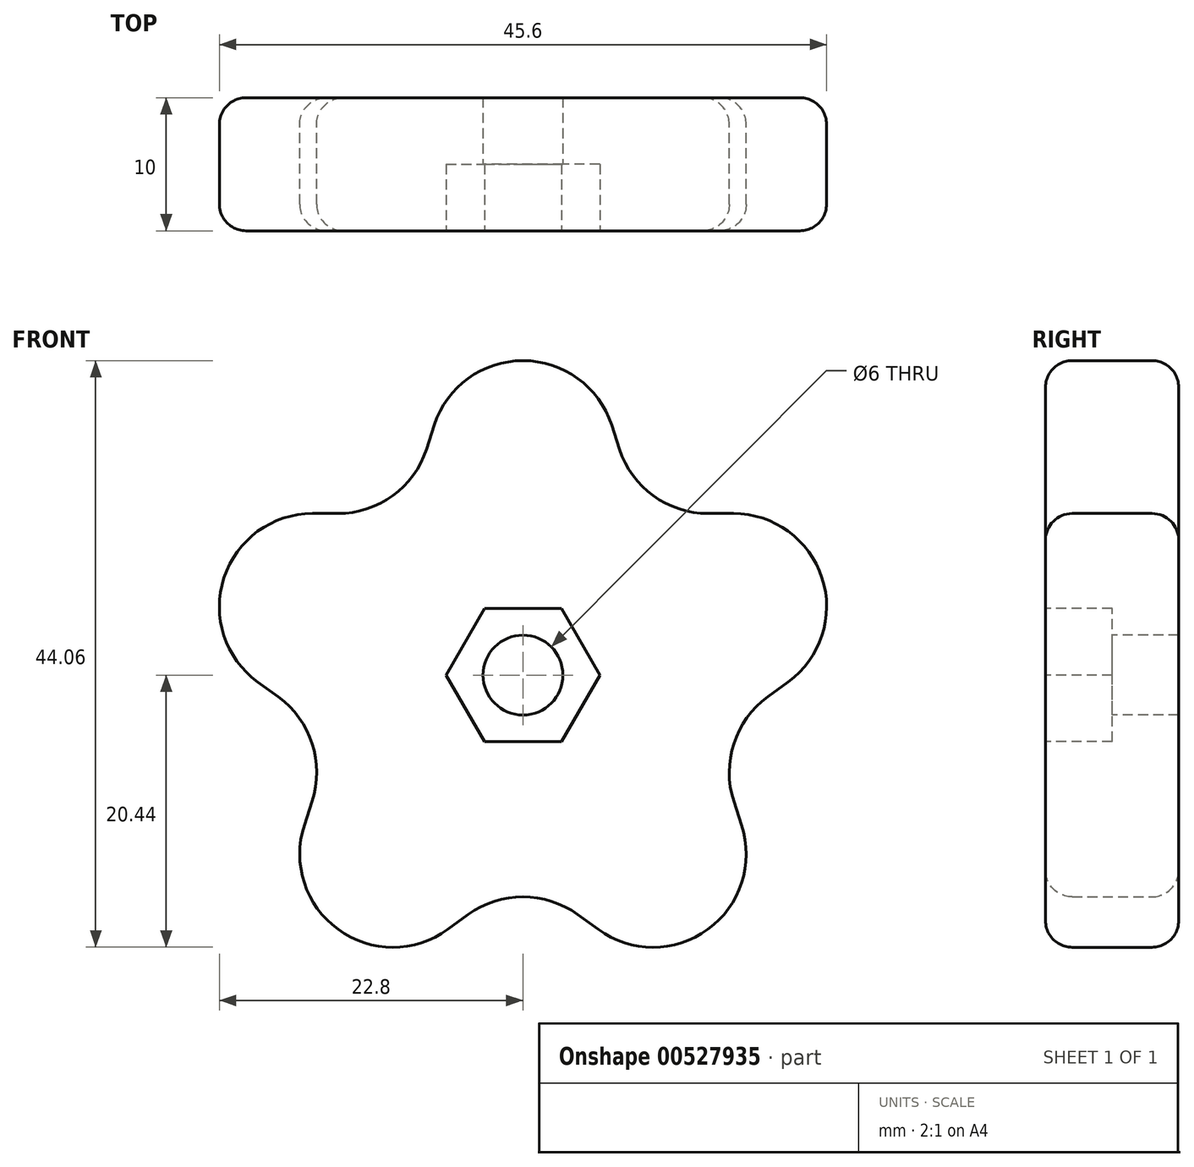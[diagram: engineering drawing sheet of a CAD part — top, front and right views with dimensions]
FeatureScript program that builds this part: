
annotation { "Feature Type Name" : "Feature", "Feature Type Description" : "" }
export const myFeature = defineFeature(function(context is Context, id is Id, definition is map)
    precondition{}
    {
        {
            var Q0;
            Q0=qCreatedBy(makeId("Front.planeOp"),FACE);
            var sketch = newSketch(context, id + "F0", { "sketchPlane" : qUnion([Q0])});
            skCircle(sketch, "E0.cCircle", {"center": v(0, 0) * mm, "radius": 39.27 * mm, "construction": true});
            skLineSegment(sketch, "E1", {"start": v(0, 39.27) * mm, "end": v(-8.82, 12.14) * mm});
            skLineSegment(sketch, "E2", {"start": v(-37.35, 12.14) * mm, "end": v(-8.82, 12.14) * mm});
            skLineSegment(sketch, "E3", {"start": v(0, 39.27) * mm, "end": v(8.82, 12.14) * mm});
            skLineSegment(sketch, "E4", {"start": v(23.08, -31.77) * mm, "end": v(0, -15) * mm});
            skLineSegment(sketch, "E5", {"start": v(-23.08, -31.77) * mm, "end": v(0, -15) * mm});
            skLineSegment(sketch, "E6.trimOffspring", {"start": v(-14.27, -4.64) * mm, "end": v(-37.35, 12.14) * mm});
            skLineSegment(sketch, "E7.trimOffspring", {"start": v(14.27, -4.64) * mm, "end": v(37.35, 12.14) * mm});
            skLineSegment(sketch, "E8.trimOffspring", {"start": v(14.27, -4.64) * mm, "end": v(23.08, -31.77) * mm});
            skLineSegment(sketch, "E9.trimOffspring", {"start": v(8.82, 12.14) * mm, "end": v(37.35, 12.14) * mm});
            skLineSegment(sketch, "E10.trimOffspring", {"start": v(-14.27, -4.64) * mm, "end": v(-23.08, -31.77) * mm});
            skCircle(sketch, "E11", {"center": v(0, 0) * mm, "radius": 15 * mm});
            skSolve(sketch);
        }
        {
            var Q0;
            {var subQ0=sQuery(id+"F0.wireOp",EDGE,"E7.trimOffspring");Q0=makeQuery(id+"F0.imprint","IMPRINT",FACE,{"disambiguationData":[TD([[makeQuery(id+"F0.imprint","IMPRINT",EDGE,{"derivedFrom":subQ0}),1.0]])]});}
            var Q1;
            {var subQ0=sQuery(id+"F0.wireOp",EDGE,"E1");Q1=makeQuery(id+"F0.imprint","IMPRINT",FACE,{"disambiguationData":[TD([[makeQuery(id+"F0.imprint","IMPRINT",EDGE,{"derivedFrom":subQ0}),1.0]])]});}
            var Q2;
            {var subQ0=sQuery(id+"F0.wireOp",EDGE,"E2");Q2=makeQuery(id+"F0.imprint","IMPRINT",FACE,{"disambiguationData":[TD([[makeQuery(id+"F0.imprint","IMPRINT",EDGE,{"derivedFrom":subQ0}),-1.0]])]});}
            var Q3;
            {var subQ0=sQuery(id+"F0.wireOp",EDGE,"E11");var subQ4=makeQuery(id+"F0.imprint","INTERSECT",VERTEX,{"derivedFrom":[sQuery(id+"F0.wireOp",EDGE,"E1"),sQuery(id+"F0.wireOp",EDGE,"E2"),subQ0]});Q3=makeQuery(id+"F0.imprint","IMPRINT",FACE,{"disambiguationData":[TD([[makeQuery(id+"F0.imprint","IMPRINT",EDGE,{"disambiguationData":[TD([[subQ4,1.0]])],"derivedFrom":subQ0}),1.0]])]});}
            var Q4;
            {var subQ0=sQuery(id+"F0.wireOp",EDGE,"E5");Q4=makeQuery(id+"F0.imprint","IMPRINT",FACE,{"disambiguationData":[TD([[makeQuery(id+"F0.imprint","IMPRINT",EDGE,{"derivedFrom":subQ0}),1.0]])]});}
            var Q5;
            {var subQ0=sQuery(id+"F0.wireOp",EDGE,"E4");Q5=makeQuery(id+"F0.imprint","IMPRINT",FACE,{"disambiguationData":[TD([[makeQuery(id+"F0.imprint","IMPRINT",EDGE,{"derivedFrom":subQ0}),-1.0]])]});}
            extrude(context, id + "F1", {"entities" : qUnion([Q0, Q1, Q2, Q3, Q4, Q5]), "depth" : 10 * mm, "offsetDistance" : 25 * mm});
        }
        {
            var Q0;
            Q0=makeQuery(id+"F1.opExtrude","SWEPT_EDGE",EDGE,{"disambiguationData":[OSD([sQuery(id+"F0.wireOp",EDGE,"E1"),sQuery(id+"F0.wireOp",EDGE,"E3")])]});
            var Q1;
            Q1=makeQuery(id+"F1.opExtrude","SWEPT_EDGE",EDGE,{"disambiguationData":[OSD([sQuery(id+"F0.wireOp",EDGE,"E7.trimOffspring"),sQuery(id+"F0.wireOp",EDGE,"E9.trimOffspring")])]});
            var Q2;
            Q2=makeQuery(id+"F1.opExtrude","SWEPT_EDGE",EDGE,{"disambiguationData":[OSD([sQuery(id+"F0.wireOp",EDGE,"E4"),sQuery(id+"F0.wireOp",EDGE,"E8.trimOffspring")])]});
            var Q3;
            Q3=makeQuery(id+"F1.opExtrude","SWEPT_EDGE",EDGE,{"disambiguationData":[OSD([sQuery(id+"F0.wireOp",EDGE,"E2"),sQuery(id+"F0.wireOp",EDGE,"E6.trimOffspring")])]});
            var Q4;
            Q4=makeQuery(id+"F1.opExtrude","SWEPT_EDGE",EDGE,{"disambiguationData":[OSD([sQuery(id+"F0.wireOp",EDGE,"E5"),sQuery(id+"F0.wireOp",EDGE,"E10.trimOffspring")])]});
            var Q5;
            Q5=makeQuery(id+"F1.opExtrude","SWEPT_EDGE",EDGE,{"disambiguationData":[OSD([sQuery(id+"F0.wireOp",EDGE,"E6.trimOffspring"),sQuery(id+"F0.wireOp",EDGE,"E10.trimOffspring"),sQuery(id+"F0.wireOp",EDGE,"E11")])]});
            var Q6;
            Q6=makeQuery(id+"F1.opExtrude","SWEPT_EDGE",EDGE,{"disambiguationData":[OSD([sQuery(id+"F0.wireOp",EDGE,"E4"),sQuery(id+"F0.wireOp",EDGE,"E5"),sQuery(id+"F0.wireOp",EDGE,"E11")])]});
            var Q7;
            Q7=makeQuery(id+"F1.opExtrude","SWEPT_EDGE",EDGE,{"disambiguationData":[OSD([sQuery(id+"F0.wireOp",EDGE,"E7.trimOffspring"),sQuery(id+"F0.wireOp",EDGE,"E8.trimOffspring"),sQuery(id+"F0.wireOp",EDGE,"E11")])]});
            var Q8;
            Q8=makeQuery(id+"F1.opExtrude","SWEPT_EDGE",EDGE,{"disambiguationData":[OSD([sQuery(id+"F0.wireOp",EDGE,"E3"),sQuery(id+"F0.wireOp",EDGE,"E9.trimOffspring"),sQuery(id+"F0.wireOp",EDGE,"E11")])]});
            var Q9;
            Q9=makeQuery(id+"F1.opExtrude","SWEPT_EDGE",EDGE,{"disambiguationData":[OSD([sQuery(id+"F0.wireOp",EDGE,"E1"),sQuery(id+"F0.wireOp",EDGE,"E2"),sQuery(id+"F0.wireOp",EDGE,"E11")])]});
            fillet(context, id + "F2", {"entities" : qUnion([Q0, Q1, Q2, Q3, Q4, Q5, Q6, Q7, Q8, Q9]), "radius" : 7 * mm, "tangentPropagation" : true, "allowEdgeOverflow" : false});
        }
        {
            var Q0;
            Q0=makeQuery(id+"F1.opExtrude","CAP_FACE",FACE,{"disambiguationData":[OSD([sQuery(id+"F0.wireOp",EDGE,"E1"),sQuery(id+"F0.wireOp",EDGE,"E2"),sQuery(id+"F0.wireOp",EDGE,"E3"),sQuery(id+"F0.wireOp",EDGE,"E4"),sQuery(id+"F0.wireOp",EDGE,"E5"),sQuery(id+"F0.wireOp",EDGE,"E6.trimOffspring"),sQuery(id+"F0.wireOp",EDGE,"E7.trimOffspring"),sQuery(id+"F0.wireOp",EDGE,"E8.trimOffspring"),sQuery(id+"F0.wireOp",EDGE,"E9.trimOffspring"),sQuery(id+"F0.wireOp",EDGE,"E10.trimOffspring")])],"isStart":false});
            var sketch = newSketch(context, id + "F3", { "sketchPlane" : qUnion([Q0])});
            skCircle(sketch, "E12.cCircle", {"center": v(0, 0) * mm, "radius": 5 * mm, "construction": true});
            skLineSegment(sketch, "E12.0", {"start": v(-2.89, 5) * mm, "end": v(2.89, 5) * mm});
            skLineSegment(sketch, "E12.1", {"start": v(2.89, 5) * mm, "end": v(5.77, 0) * mm});
            skLineSegment(sketch, "E12.2", {"start": v(5.77, 0) * mm, "end": v(2.89, -5) * mm});
            skLineSegment(sketch, "E12.3", {"start": v(2.89, -5) * mm, "end": v(-2.89, -5) * mm});
            skLineSegment(sketch, "E12.4", {"start": v(-2.89, -5) * mm, "end": v(-5.77, 0) * mm});
            skLineSegment(sketch, "E12.5", {"start": v(-5.77, 0) * mm, "end": v(-2.89, 5) * mm});
            skPoint(sketch, "E12.0.midPoint", {"position": v(0, 5) * mm});
            skSolve(sketch);
        }
        {
            var Q0;
            Q0=makeQuery(id+"F3.imprint","IMPRINT",FACE,{"disambiguationData":[TD([[makeQuery(id+"F3.imprint","IMPRINT",EDGE,{"derivedFrom":sQuery(id+"F3.wireOp",EDGE,"E12.0")}),-1.0]])]});
            extrude(context, id + "F4", {"entities" : qUnion([Q0]), "operationType" : NewBodyOperationType.REMOVE, "oppositeDirection" : true, "depth" : 5 * mm, "offsetDistance" : 25 * mm});
        }
        {
            var Q0;
            Q0=makeQuery(id+"F4.boolean.opBoolean","COPY",FACE,{"derivedFrom":makeQuery(id+"F4.opExtrude","CAP_FACE",FACE,{"disambiguationData":[OSD([sQuery(id+"F3.wireOp",EDGE,"E12.0"),sQuery(id+"F3.wireOp",EDGE,"E12.1"),sQuery(id+"F3.wireOp",EDGE,"E12.2"),sQuery(id+"F3.wireOp",EDGE,"E12.3"),sQuery(id+"F3.wireOp",EDGE,"E12.4"),sQuery(id+"F3.wireOp",EDGE,"E12.5")])],"isStart":false})});
            var sketch = newSketch(context, id + "F5", { "sketchPlane" : qUnion([Q0])});
            skCircle(sketch, "E13", {"center": v(0, 0) * mm, "radius": 3 * mm});
            skSolve(sketch);
        }
        {
            var Q0;
            Q0=makeQuery(id+"F5.imprint","IMPRINT",FACE,{"disambiguationData":[TD([[makeQuery(id+"F5.imprint","IMPRINT",EDGE,{"derivedFrom":sQuery(id+"F5.wireOp",EDGE,"E13")}),1.0]])]});
            extrude(context, id + "F6", {"entities" : qUnion([Q0]), "operationType" : NewBodyOperationType.REMOVE, "endBound" : BoundingType.UP_TO_NEXT, "oppositeDirection" : true, "depth" : 25 * mm, "offsetDistance" : 25 * mm});
        }
        {
            var Q0;
            {var subQ0=sQuery(id+"F0.wireOp",EDGE,"E3");var subQ1=sQuery(id+"F0.wireOp",EDGE,"E1");Q0=makeQuery(id+"F2.opFillet","BLEND_EDGE",EDGE,{"blendedFrom":[makeQuery(id+"F1.opExtrude","SWEPT_EDGE",EDGE,{"disambiguationData":[OSD([subQ1,subQ0])]}),makeQuery(id+"F1.opExtrude","CAP_FACE",FACE,{"disambiguationData":[OSD([subQ1,sQuery(id+"F0.wireOp",EDGE,"E2"),subQ0,sQuery(id+"F0.wireOp",EDGE,"E4"),sQuery(id+"F0.wireOp",EDGE,"E5"),sQuery(id+"F0.wireOp",EDGE,"E6.trimOffspring"),sQuery(id+"F0.wireOp",EDGE,"E7.trimOffspring"),sQuery(id+"F0.wireOp",EDGE,"E8.trimOffspring"),sQuery(id+"F0.wireOp",EDGE,"E9.trimOffspring"),sQuery(id+"F0.wireOp",EDGE,"E10.trimOffspring")])],"isStart":false})],"blendedInto":[makeQuery(id+"F1.opExtrude","CAP_FACE",FACE,{"disambiguationData":[OSD([subQ1,sQuery(id+"F0.wireOp",EDGE,"E2"),subQ0,sQuery(id+"F0.wireOp",EDGE,"E4"),sQuery(id+"F0.wireOp",EDGE,"E5"),sQuery(id+"F0.wireOp",EDGE,"E6.trimOffspring"),sQuery(id+"F0.wireOp",EDGE,"E7.trimOffspring"),sQuery(id+"F0.wireOp",EDGE,"E8.trimOffspring"),sQuery(id+"F0.wireOp",EDGE,"E9.trimOffspring"),sQuery(id+"F0.wireOp",EDGE,"E10.trimOffspring")])],"isStart":false})]});}
            var Q1;
            {var subQ0=sQuery(id+"F0.wireOp",EDGE,"E9.trimOffspring");var subQ1=sQuery(id+"F0.wireOp",EDGE,"E3");Q1=makeQuery(id+"F2.opFillet","BLEND_EDGE",EDGE,{"blendedFrom":[makeQuery(id+"F1.opExtrude","SWEPT_EDGE",EDGE,{"disambiguationData":[OSD([subQ1,subQ0,sQuery(id+"F0.wireOp",EDGE,"E11")])]}),makeQuery(id+"F1.opExtrude","CAP_FACE",FACE,{"disambiguationData":[OSD([sQuery(id+"F0.wireOp",EDGE,"E1"),sQuery(id+"F0.wireOp",EDGE,"E2"),subQ1,sQuery(id+"F0.wireOp",EDGE,"E4"),sQuery(id+"F0.wireOp",EDGE,"E5"),sQuery(id+"F0.wireOp",EDGE,"E6.trimOffspring"),sQuery(id+"F0.wireOp",EDGE,"E7.trimOffspring"),sQuery(id+"F0.wireOp",EDGE,"E8.trimOffspring"),subQ0,sQuery(id+"F0.wireOp",EDGE,"E10.trimOffspring")])],"isStart":false})],"blendedInto":[makeQuery(id+"F1.opExtrude","CAP_FACE",FACE,{"disambiguationData":[OSD([sQuery(id+"F0.wireOp",EDGE,"E1"),sQuery(id+"F0.wireOp",EDGE,"E2"),subQ1,sQuery(id+"F0.wireOp",EDGE,"E4"),sQuery(id+"F0.wireOp",EDGE,"E5"),sQuery(id+"F0.wireOp",EDGE,"E6.trimOffspring"),sQuery(id+"F0.wireOp",EDGE,"E7.trimOffspring"),sQuery(id+"F0.wireOp",EDGE,"E8.trimOffspring"),subQ0,sQuery(id+"F0.wireOp",EDGE,"E10.trimOffspring")])],"isStart":false})]});}
            var Q2;
            {var subQ0=sQuery(id+"F0.wireOp",EDGE,"E3");var subQ1=sQuery(id+"F0.wireOp",EDGE,"E1");Q2=makeQuery(id+"F2.opFillet","BLEND_EDGE",EDGE,{"blendedFrom":[makeQuery(id+"F1.opExtrude","SWEPT_EDGE",EDGE,{"disambiguationData":[OSD([subQ1,subQ0])]}),makeQuery(id+"F1.opExtrude","CAP_FACE",FACE,{"disambiguationData":[OSD([subQ1,sQuery(id+"F0.wireOp",EDGE,"E2"),subQ0,sQuery(id+"F0.wireOp",EDGE,"E4"),sQuery(id+"F0.wireOp",EDGE,"E5"),sQuery(id+"F0.wireOp",EDGE,"E6.trimOffspring"),sQuery(id+"F0.wireOp",EDGE,"E7.trimOffspring"),sQuery(id+"F0.wireOp",EDGE,"E8.trimOffspring"),sQuery(id+"F0.wireOp",EDGE,"E9.trimOffspring"),sQuery(id+"F0.wireOp",EDGE,"E10.trimOffspring")])],"isStart":true})],"blendedInto":[makeQuery(id+"F1.opExtrude","CAP_FACE",FACE,{"disambiguationData":[OSD([subQ1,sQuery(id+"F0.wireOp",EDGE,"E2"),subQ0,sQuery(id+"F0.wireOp",EDGE,"E4"),sQuery(id+"F0.wireOp",EDGE,"E5"),sQuery(id+"F0.wireOp",EDGE,"E6.trimOffspring"),sQuery(id+"F0.wireOp",EDGE,"E7.trimOffspring"),sQuery(id+"F0.wireOp",EDGE,"E8.trimOffspring"),sQuery(id+"F0.wireOp",EDGE,"E9.trimOffspring"),sQuery(id+"F0.wireOp",EDGE,"E10.trimOffspring")])],"isStart":true})]});}
            var Q3;
            Q3=makeQuery(id+"F1.opExtrude","CAP_EDGE",EDGE,{"disambiguationData":[OSD([sQuery(id+"F0.wireOp",EDGE,"E3")])],"isStart":true});
            fillet(context, id + "F7", {"entities" : qUnion([Q0, Q1, Q2, Q3]), "radius" : 2 * mm, "tangentPropagation" : true, "allowEdgeOverflow" : false});
        }
    });
